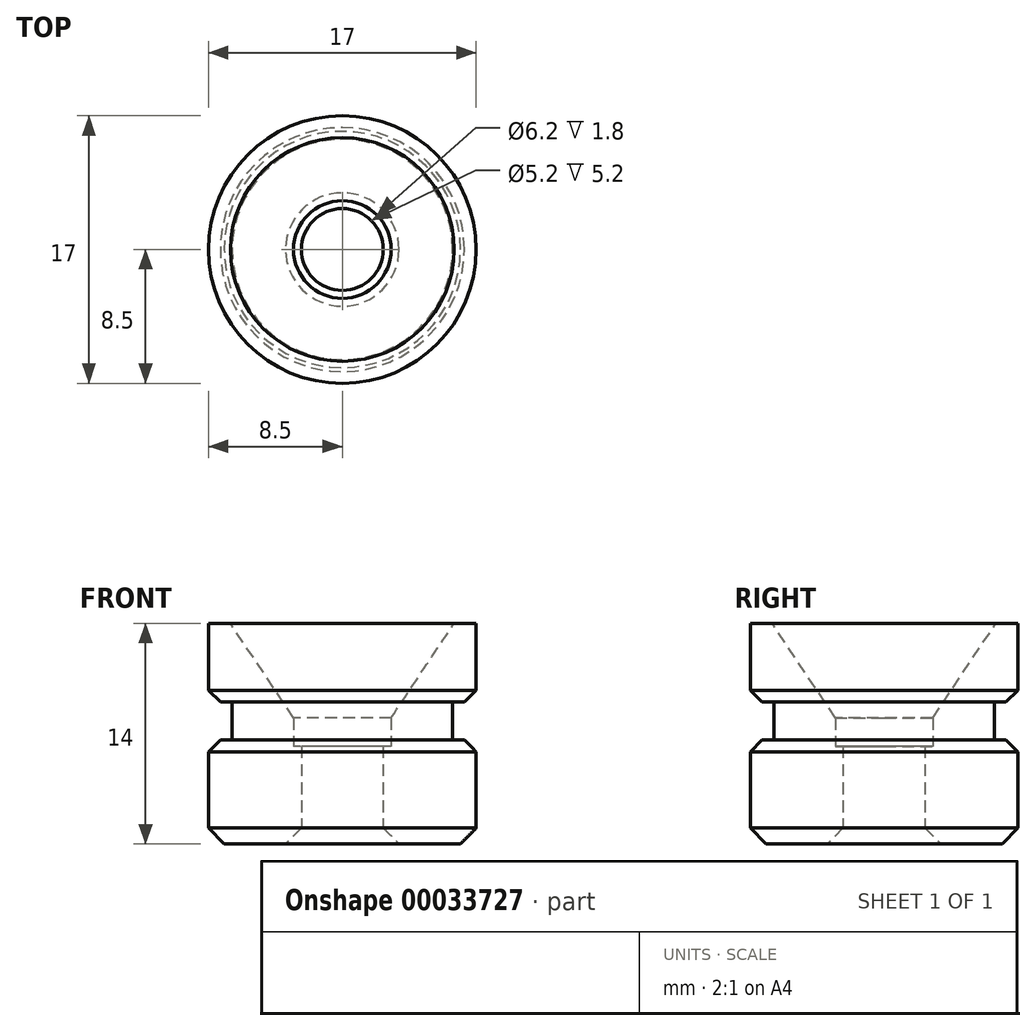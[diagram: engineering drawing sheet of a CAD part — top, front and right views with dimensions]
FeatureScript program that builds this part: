
annotation { "Feature Type Name" : "Feature", "Feature Type Description" : "" }
export const myFeature = defineFeature(function(context is Context, id is Id, definition is map)
    precondition{}
    {
        {
            var Q0;
            Q0=qCreatedBy(makeId("Top.planeOp"),FACE);
            var sketch = newSketch(context, id + "F0", { "sketchPlane" : qUnion([Q0])});
            skCircle(sketch, "E0", {"center": v(0, 0) * mm, "radius": 2.6 * mm});
            skCircle(sketch, "E1", {"center": v(0, 0) * mm, "radius": 8.5 * mm});
            skCircle(sketch, "E2", {"center": v(0, 0) * mm, "radius": 3.1 * mm});
            skCircle(sketch, "E3", {"center": v(0, 0) * mm, "radius": 7 * mm});
            skSolve(sketch);
        }
        {
            var Q0;
            Q0 = qSketchRegion(id + "F0", true);
            extrude(context, id + "F1", {"entities" : qUnion([Q0]), "depth" : 6.6 * mm, "offsetDistance" : 25 * mm});
        }
        {
            var Q0;
            Q0=makeQuery(id+"F0.imprint","IMPRINT",FACE,{"disambiguationData":[TD([[makeQuery(id+"F0.imprint","IMPRINT",EDGE,{"derivedFrom":sQuery(id+"F0.wireOp",EDGE,"E2")}),-1.0]])]});
            extrude(context, id + "F2", {"entities" : qUnion([Q0]), "operationType" : NewBodyOperationType.ADD, "depth" : 9 * mm, "offsetDistance" : 25 * mm});
        }
        {
            var Q0;
            Q0=makeQuery(id+"F2.opExtrude","CAP_FACE",FACE,{"disambiguationData":[OSD([sQuery(id+"F0.wireOp",EDGE,"E2"),sQuery(id+"F0.wireOp",EDGE,"E3")])],"isStart":false});
            var sketch = newSketch(context, id + "F3", { "sketchPlane" : qUnion([Q0])});
            skCircle(sketch, "E4.1.0", {"center": v(0, 0) * mm, "radius": 8.5 * mm});
            skCircle(sketch, "E5.0", {"center": v(0, 0) * mm, "radius": 7 * mm});
            skCircle(sketch, "E6.0", {"center": v(0, 0) * mm, "radius": 3.1 * mm});
            skSolve(sketch);
        }
        {
            var Q0;
            Q0 = qSketchRegion(id + "F3", true);
            var Q1;
            Q1=makeQuery(id+"F3.imprint","IMPRINT",FACE,{"disambiguationData":[TD([[makeQuery(id+"F3.imprint","IMPRINT",EDGE,{"derivedFrom":sQuery(id+"F3.wireOp",EDGE,"E5.0")}),1.0]])]});
            extrude(context, id + "F4", {"entities" : qUnion([Q0, Q1]), "operationType" : NewBodyOperationType.ADD, "depth" : 5 * mm, "offsetDistance" : 25 * mm});
        }
        {
            var Q0;
            Q0=makeQuery(id+"F0.imprint","IMPRINT",FACE,{"disambiguationData":[TD([[makeQuery(id+"F0.imprint","IMPRINT",EDGE,{"derivedFrom":sQuery(id+"F0.wireOp",EDGE,"E0")}),-1.0]])]});
            extrude(context, id + "F5", {"entities" : qUnion([Q0]), "operationType" : NewBodyOperationType.ADD, "depth" : 6.2 * mm, "offsetDistance" : 25 * mm});
        }
        {
            var Q0;
            Q0=makeQuery(id+"F5.opExtrude","CAP_EDGE",EDGE,{"disambiguationData":[OSD([sQuery(id+"F0.wireOp",EDGE,"E0")])],"isStart":true});
            var Q1;
            Q1=makeQuery(id+"F1.opExtrude","CAP_EDGE",EDGE,{"disambiguationData":[OSD([sQuery(id+"F0.wireOp",EDGE,"E1")])],"isStart":true});
            chamfer(context, id + "F6", {"entities" : qUnion([Q0, Q1]), "width" : 1 * mm, "tangentPropagation" : true});
        }
        {
            var Q0;
            Q0=makeQuery(id+"F4.opExtrude","CAP_EDGE",EDGE,{"disambiguationData":[OSD([sQuery(id+"F3.wireOp",EDGE,"E6.0")])],"isStart":false});
            chamfer(context, id + "F7", {"entities" : qUnion([Q0]), "chamferType" : ChamferType.TWO_OFFSETS, "width1" : 6 * mm, "oppositeDirection" : false, "width2" : 4 * mm, "tangentPropagation" : true});
        }
        {
            var Q0;
            Q0=makeQuery(id+"F2.opExtrude","CAP_EDGE",EDGE,{"disambiguationData":[OSD([sQuery(id+"F0.wireOp",EDGE,"E3")])],"isStart":false});
            var Q1;
            Q1=makeQuery(id+"F1.opExtrude","CAP_EDGE",EDGE,{"disambiguationData":[OSD([sQuery(id+"F0.wireOp",EDGE,"E3")])],"isStart":false});
            var Q2;
            Q2=makeQuery(id+"F1.opExtrude","CAP_EDGE",EDGE,{"disambiguationData":[OSD([sQuery(id+"F0.wireOp",EDGE,"E1")])],"isStart":false});
            var Q3;
            Q3=makeQuery(id+"F4.opExtrude","CAP_EDGE",EDGE,{"disambiguationData":[OSD([sQuery(id+"F3.wireOp",EDGE,"E4.1.0")])],"isStart":true});
            chamfer(context, id + "F8", {"entities" : qUnion([Q0, Q1, Q2, Q3]), "width" : 0.75 * mm, "tangentPropagation" : true});
        }
    });
